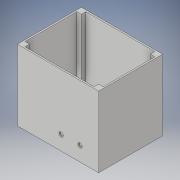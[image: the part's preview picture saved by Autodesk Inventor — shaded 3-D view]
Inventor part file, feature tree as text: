
AUTODESK INVENTOR PART (.ipt)
format: ipt  version: 2018 (Build 220112000, 112)  size: 173,056 bytes
history: native  units: in
note: dims shown in document units (in); Inventor stores cm internally (conversion verified against a paired STEP export)
features: extrude x6, sketch x6
ambient origin geometry x8: Origin, YZ Plane, XZ Plane, XY Plane, X Axis, Y Axis, Z Axis, Center Point
bodies: Solid1 (feature_tree)
feature tree (12):
  extrude  "Extrusion1"  Depth=3.701in
  extrude  "Extrusion2"  Depth=4.527in
  extrude  "Extrusion3"  Depth=0.354in
  extrude  "Extrusion6"  Depth=0.354in
  extrude  "Extrusion7"  Depth=4.0in TaperAngle=0.0deg
  extrude  "Extrusion8"  Depth=0.164in
  sketch  "Sketch1"  dims[d0=4.705in d1=3.701in]
  sketch  "Sketch2"  dims[d2=0.089in d3=0.0in d4=4.527in]
  sketch  "Sketch3"  dims[d5=3.523in d6=0.354in]
  sketch  "Sketch7"  dims[d7=0.354in d10=0.354in]
  sketch  "Sketch8"  dims[d11=0.354in d14=4.0in d15=0.0in]
  sketch  "Sketch9"  dims[d18=0.164in d19=0.164in d20=0.0in d21=0.0in d57=0.112in d58=0.112in d59=0.112in d60=0.112in d61=2.598in d62=0.787in d63=0.118in d64=0.118in d65=0.118in d66=0.118in d67=0.0in d68=0.0in d71=0.25in d72=0.25in d73=0.0in d74=0.0in d79=0.25in d80=0.25in d81=0.0in d82=0.0in]
